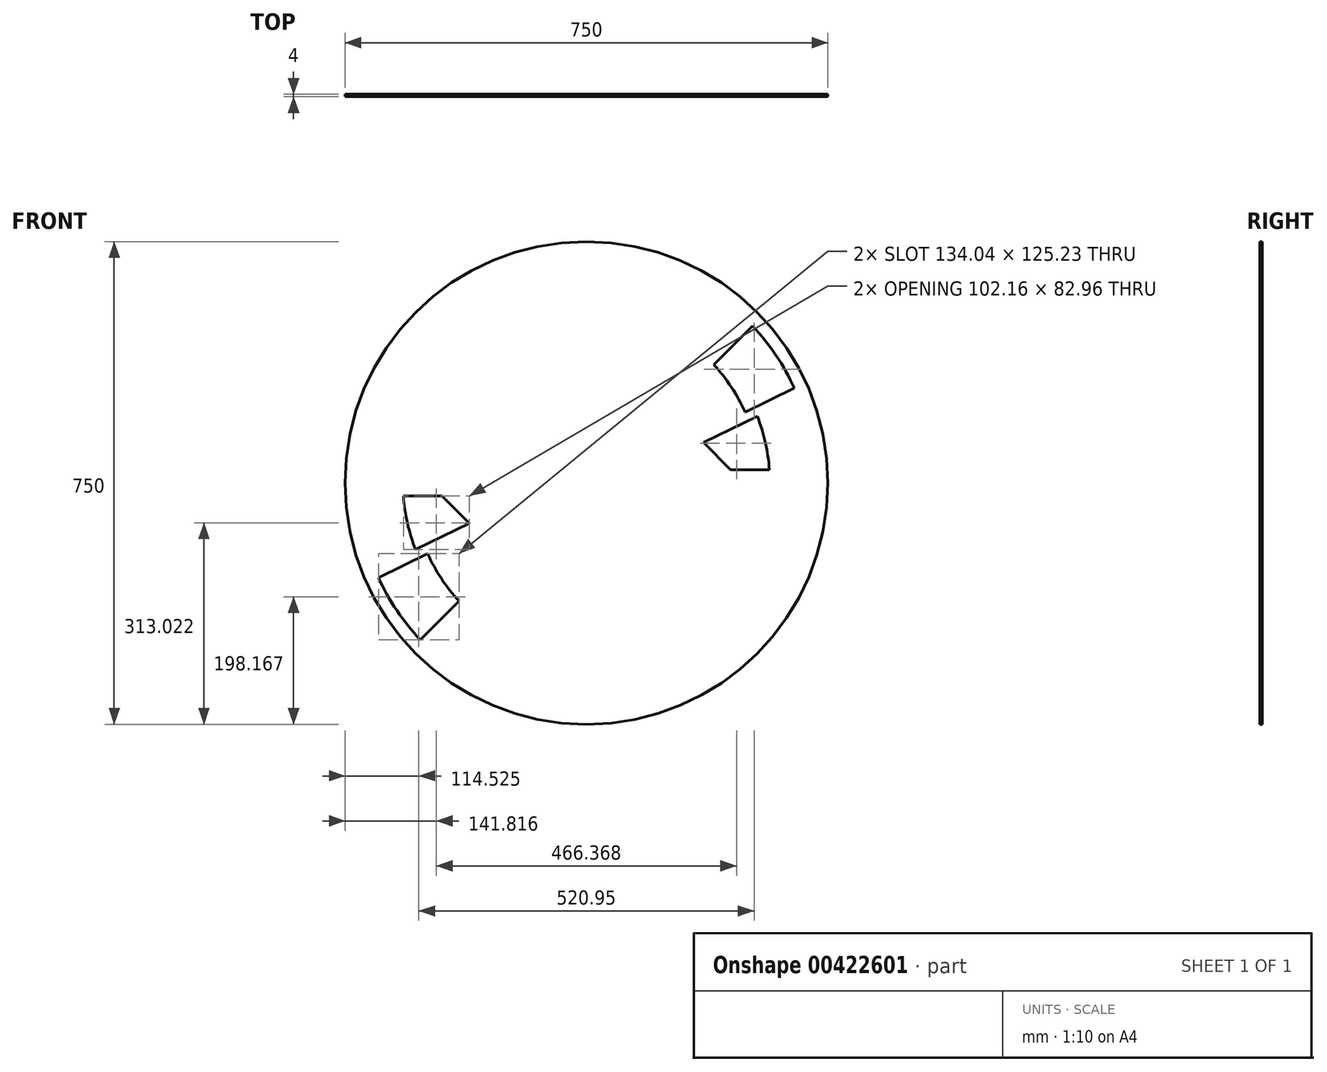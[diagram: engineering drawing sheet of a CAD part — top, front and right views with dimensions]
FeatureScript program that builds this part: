
annotation { "Feature Type Name" : "Feature", "Feature Type Description" : "" }
export const myFeature = defineFeature(function(context is Context, id is Id, definition is map)
    precondition{}
    {
        {
            var Q0;
            Q0=qCreatedBy(makeId("Front.planeOp"),FACE);
            var sketch = newSketch(context, id + "F0", { "sketchPlane" : qUnion([Q0])});
            skLineSegment(sketch, "E0", {"start": v(-123, -114.98) * mm, "end": v(-227.04, -10.5) * mm});
            skLineSegment(sketch, "E1", {"start": v(-227.04, -10.5) * mm, "end": v(-227.04, 10.5) * mm});
            skLineSegment(sketch, "E2", {"start": v(-227.04, 10.5) * mm, "end": v(-123.04, 115.02) * mm});
            skLineSegment(sketch, "E3", {"start": v(-123.04, 115.02) * mm, "end": v(122.96, 115.02) * mm});
            skLineSegment(sketch, "E4", {"start": v(122.96, 115.02) * mm, "end": v(226.96, 10.5) * mm});
            skLineSegment(sketch, "E5", {"start": v(226.96, 10.5) * mm, "end": v(226.96, -10.5) * mm});
            skLineSegment(sketch, "E6", {"start": v(226.96, -10.5) * mm, "end": v(123, -115.06) * mm});
            skLineSegment(sketch, "E7", {"start": v(123, -115.06) * mm, "end": v(-123, -114.98) * mm});
            skPoint(sketch, "E8.startSnap0", {"position": v(226.96, 0) * mm});
            skPoint(sketch, "E8.endSnap0", {"position": v(-227.04, 0) * mm});
            skPoint(sketch, "E9.endSnap0", {"position": v(0, -115.02) * mm});
            skPoint(sketch, "E10", {"position": v(0, 0) * mm});
            skLineSegment(sketch, "E11", {"start": v(0, -317.44) * mm, "end": v(0, 323.8) * mm, "construction": true});
            skLineSegment(sketch, "E12", {"start": v(439.72, 0) * mm, "end": v(-379.77, 0) * mm, "construction": true});
            skPoint(sketch, "E13", {"position": v(0, 115.02) * mm});
            skSolve(sketch);
        }
        {
            var Q0;
            Q0=qCreatedBy(makeId("Front.planeOp"),FACE);
            var sketch = newSketch(context, id + "F1", { "sketchPlane" : qUnion([Q0])});
            skLineSegment(sketch, "E14.bottom", {"start": v(-420, 150) * mm, "end": v(-250, 150) * mm});
            skLineSegment(sketch, "E14.top", {"start": v(-420, 350) * mm, "end": v(-250, 350) * mm});
            skLineSegment(sketch, "E14.left", {"start": v(-420, 150) * mm, "end": v(-420, 350) * mm});
            skLineSegment(sketch, "E14.right", {"start": v(-250, 150) * mm, "end": v(-250, 350) * mm});
            skPoint(sketch, "E15.0", {"position": v(0, -115.03) * mm});
            skPoint(sketch, "E16.0", {"position": v(-195.63, 123.06) * mm});
            skPoint(sketch, "E17.0", {"position": v(-424.13, 9.56) * mm});
            skPoint(sketch, "E18.0", {"position": v(225.44, 0) * mm});
            skLineSegment(sketch, "E19", {"start": v(0, -244.95) * mm, "end": v(0, 298.47) * mm, "construction": true});
            skLineSegment(sketch, "E20", {"start": v(303.44, 0) * mm, "end": v(-317.51, 0) * mm, "construction": true});
            skLineSegment(sketch, "E21.MirrorCS", {"start": v(250, 150) * mm, "end": v(250, 350) * mm});
            skLineSegment(sketch, "E22.MirrorCS", {"start": v(420, 150) * mm, "end": v(250, 150) * mm});
            skLineSegment(sketch, "E23.MirrorCS", {"start": v(420, 150) * mm, "end": v(420, 350) * mm});
            skLineSegment(sketch, "E24.MirrorCS", {"start": v(420, 350) * mm, "end": v(250, 350) * mm});
            skLineSegment(sketch, "E25.MirrorCS", {"start": v(-420, -150) * mm, "end": v(-250, -150) * mm});
            skLineSegment(sketch, "E26.MirrorCS", {"start": v(-420, -150) * mm, "end": v(-420, -350) * mm});
            skLineSegment(sketch, "E27.MirrorCS", {"start": v(-420, -350) * mm, "end": v(-250, -350) * mm});
            skLineSegment(sketch, "E28.MirrorCS", {"start": v(-250, -150) * mm, "end": v(-250, -350) * mm});
            skLineSegment(sketch, "E29.MirrorCS", {"start": v(250, -150) * mm, "end": v(250, -350) * mm});
            skLineSegment(sketch, "E30.MirrorCS", {"start": v(420, -350) * mm, "end": v(250, -350) * mm});
            skLineSegment(sketch, "E31.MirrorCS", {"start": v(420, -150) * mm, "end": v(420, -350) * mm});
            skLineSegment(sketch, "E32.MirrorCS", {"start": v(420, -150) * mm, "end": v(250, -150) * mm});
            skPoint(sketch, "E33", {"position": v(0, 0) * mm});
            skSolve(sketch);
        }
        {
            var Q0;
            Q0=qCreatedBy(makeId("Front.planeOp"),FACE);
            var sketch = newSketch(context, id + "F2", { "sketchPlane" : qUnion([Q0])});
            skCircle(sketch, "E34", {"center": v(0, 0) * mm, "radius": 375 * mm});
            skLineSegment(sketch, "E35", {"start": v(-224.15, 20.5) * mm, "end": v(-129.63, 115.49) * mm, "construction": true});
            skLineSegment(sketch, "E36", {"start": v(-129.63, 115.49) * mm, "end": v(-258, 243.85) * mm, "construction": true});
            skLineSegment(sketch, "E37", {"start": v(-224.15, 20.5) * mm, "end": v(-354.4, 20.5) * mm});
            skArc(sketch, "E38", {"start": v(-354.4, 20.5) * mm, "mid": v(325.93, -140.7) * mm, "end": v(-258, 243.85) * mm, "construction": true});
            skArc(sketch, "E39", {"start": v(-258, 243.85) * mm, "mid": v(-325.93, 140.7) * mm, "end": v(-354.4, 20.5) * mm, "construction": true});
            skLineSegment(sketch, "E40", {"start": v(0, 0) * mm, "end": v(-331.85, 331.85) * mm, "construction": true});
            skLineSegment(sketch, "E41", {"start": v(-176.89, 68) * mm, "end": v(-325.93, 140.7) * mm, "construction": true});
            skLineSegment(sketch, "E42.0", {"start": v(-171.67, 73.24) * mm, "end": v(-323.1, 147.1) * mm, "construction": true});
            skLineSegment(sketch, "E43.MirrorCS", {"start": v(-182.1, 62.75) * mm, "end": v(-252.03, 96.86) * mm, "construction": true});
            skPoint(sketch, "E44.orphan", {"position": v(-322.5, 146.81) * mm});
            skArc(sketch, "E45", {"start": v(-284.26, 20.5) * mm, "mid": v(261.25, -113.9) * mm, "end": v(-208.47, 194.33) * mm, "construction": true});
            skArc(sketch, "E46", {"start": v(-265.56, 103.46) * mm, "mid": v(-278.02, 62.68) * mm, "end": v(-284.26, 20.5) * mm, "construction": true});
            skArc(sketch, "E47", {"start": v(-260.15, 116.4) * mm, "mid": v(-262.93, 109.96) * mm, "end": v(-265.56, 103.46) * mm, "construction": true});
            skArc(sketch, "E48", {"start": v(-208.47, 194.33) * mm, "mid": v(-237.53, 157.5) * mm, "end": v(-260.15, 116.4) * mm, "construction": true});
            skArc(sketch, "E49", {"start": v(-197.86, 183.72) * mm, "mid": v(-225.3, 148.78) * mm, "end": v(-246.66, 109.81) * mm, "construction": true});
            skArc(sketch, "E50", {"start": v(-246.66, 109.81) * mm, "mid": v(-261.78, 66.13) * mm, "end": v(-269.22, 20.5) * mm, "construction": true});
            skLineSegment(sketch, "E51", {"start": v(-252.03, 96.86) * mm, "end": v(-328.65, 134.23) * mm, "construction": true});
            skArc(sketch, "E52", {"start": v(-269.22, 20.5) * mm, "mid": v(247.39, -108.16) * mm, "end": v(-197.86, 183.72) * mm, "construction": true});
            skLineSegment(sketch, "E53.MirrorCS", {"start": v(224.15, 20.5) * mm, "end": v(129.63, 115.49) * mm});
            skLineSegment(sketch, "E54.MirrorCS", {"start": v(171.67, 73.24) * mm, "end": v(323.1, 147.1) * mm});
            skLineSegment(sketch, "E55.MirrorCS", {"start": v(129.63, 115.49) * mm, "end": v(258, 243.85) * mm});
            skArc(sketch, "E56.MirrorCS", {"start": v(197.86, 183.72) * mm, "mid": v(225.3, 148.78) * mm, "end": v(246.66, 109.81) * mm});
            skArc(sketch, "E57.MirrorCS", {"start": v(208.47, 194.33) * mm, "mid": v(237.53, 157.5) * mm, "end": v(260.15, 116.4) * mm});
            skArc(sketch, "E58.MirrorCS", {"start": v(258, 243.85) * mm, "mid": v(325.93, 140.7) * mm, "end": v(354.4, 20.5) * mm});
            skLineSegment(sketch, "E59.MirrorCS", {"start": v(224.15, 20.5) * mm, "end": v(354.4, 20.5) * mm});
            skArc(sketch, "E60.MirrorCS", {"start": v(265.56, 103.46) * mm, "mid": v(278.02, 62.68) * mm, "end": v(284.26, 20.5) * mm});
            skArc(sketch, "E61.MirrorCS", {"start": v(246.66, 109.81) * mm, "mid": v(261.78, 66.13) * mm, "end": v(269.22, 20.5) * mm});
            skLineSegment(sketch, "E62.MirrorCS", {"start": v(182.1, 62.75) * mm, "end": v(252.03, 96.86) * mm});
            skLineSegment(sketch, "E63.MirrorCS", {"start": v(252.03, 96.86) * mm, "end": v(328.65, 134.23) * mm});
            skArc(sketch, "E64.MirrorCS", {"start": v(-258, -243.85) * mm, "mid": v(-325.93, -140.7) * mm, "end": v(-354.4, -20.5) * mm});
            skLineSegment(sketch, "E65.MirrorCS", {"start": v(-224.15, -20.5) * mm, "end": v(-354.4, -20.5) * mm});
            skArc(sketch, "E66.MirrorCS", {"start": v(-246.66, -109.81) * mm, "mid": v(-261.78, -66.13) * mm, "end": v(-269.22, -20.5) * mm});
            skArc(sketch, "E67.MirrorCS", {"start": v(-265.56, -103.46) * mm, "mid": v(-278.02, -62.68) * mm, "end": v(-284.26, -20.5) * mm});
            skLineSegment(sketch, "E68.MirrorCS", {"start": v(-252.03, -96.86) * mm, "end": v(-328.65, -134.23) * mm});
            skLineSegment(sketch, "E69.MirrorCS", {"start": v(-171.67, -73.24) * mm, "end": v(-323.1, -147.1) * mm});
            skLineSegment(sketch, "E70.MirrorCS", {"start": v(-182.1, -62.75) * mm, "end": v(-252.03, -96.86) * mm});
            skLineSegment(sketch, "E71.MirrorCS", {"start": v(-129.63, -115.49) * mm, "end": v(-258, -243.85) * mm});
            skArc(sketch, "E72.MirrorCS", {"start": v(-197.86, -183.72) * mm, "mid": v(-225.3, -148.78) * mm, "end": v(-246.66, -109.81) * mm});
            skArc(sketch, "E73.MirrorCS", {"start": v(-208.47, -194.33) * mm, "mid": v(-237.53, -157.5) * mm, "end": v(-260.15, -116.4) * mm});
            skLineSegment(sketch, "E74.MirrorCS", {"start": v(-224.15, -20.5) * mm, "end": v(-129.63, -115.49) * mm});
            skSolve(sketch);
        }
        {
            var Q0;
            Q0=makeQuery(id+"F2.imprint","IMPRINT",FACE,{"disambiguationData":[TD([[makeQuery(id+"F2.imprint","IMPRINT",EDGE,{"derivedFrom":sQuery(id+"F2.wireOp",EDGE,"E34")}),1.0]])]});
            var Q1;
            {var subQ3=sQuery(id+"F2.wireOp",EDGE,"E70.MirrorCS");Q1=makeQuery(id+"F2.imprint","IMPRINT",FACE,{"disambiguationData":[TD([[makeQuery(id+"F2.imprint","IMPRINT",EDGE,{"derivedFrom":subQ3}),1.0]])]});}
            var Q2;
            {var subQ5=sQuery(id+"F2.wireOp",EDGE,"E67.MirrorCS");Q2=makeQuery(id+"F2.imprint","IMPRINT",FACE,{"disambiguationData":[TD([[makeQuery(id+"F2.imprint","IMPRINT",EDGE,{"derivedFrom":subQ5}),-1.0]])]});}
            var Q3;
            {var subQ4=sQuery(id+"F2.wireOp",EDGE,"E68.MirrorCS");var subQ5=makeQuery(id+"F2.imprint","INTERSECT",VERTEX,{"derivedFrom":[sQuery(id+"F2.wireOp",EDGE,"E67.MirrorCS"),subQ4]});Q3=makeQuery(id+"F2.imprint","IMPRINT",FACE,{"disambiguationData":[TD([[makeQuery(id+"F2.imprint","IMPRINT",EDGE,{"disambiguationData":[TD([[subQ5,-1.0]])],"derivedFrom":subQ4}),1.0]])]});}
            var Q4;
            {var subQ0=sQuery(id+"F2.wireOp",EDGE,"E72.MirrorCS");Q4=makeQuery(id+"F2.imprint","IMPRINT",FACE,{"disambiguationData":[TD([[makeQuery(id+"F2.imprint","IMPRINT",EDGE,{"derivedFrom":subQ0}),1.0]])]});}
            var Q5;
            {var subQ0=sQuery(id+"F2.wireOp",EDGE,"E56.MirrorCS");Q5=makeQuery(id+"F2.imprint","IMPRINT",FACE,{"disambiguationData":[TD([[makeQuery(id+"F2.imprint","IMPRINT",EDGE,{"derivedFrom":subQ0}),1.0]])]});}
            var Q6;
            {var subQ3=sQuery(id+"F2.wireOp",EDGE,"E62.MirrorCS");Q6=makeQuery(id+"F2.imprint","IMPRINT",FACE,{"disambiguationData":[TD([[makeQuery(id+"F2.imprint","IMPRINT",EDGE,{"derivedFrom":subQ3}),1.0]])]});}
            var Q7;
            {var subQ0=sQuery(id+"F2.wireOp",EDGE,"E60.MirrorCS");Q7=makeQuery(id+"F2.imprint","IMPRINT",FACE,{"disambiguationData":[TD([[makeQuery(id+"F2.imprint","IMPRINT",EDGE,{"derivedFrom":subQ0}),-1.0]])]});}
            var Q8;
            {var subQ1=sQuery(id+"F2.wireOp",EDGE,"E54.MirrorCS");var subQ5=sQuery(id+"F2.wireOp",EDGE,"E58.MirrorCS");var subQ6=makeQuery(id+"F2.imprint","INTERSECT",VERTEX,{"derivedFrom":[subQ1,subQ5]});Q8=makeQuery(id+"F2.imprint","IMPRINT",FACE,{"disambiguationData":[TD([[makeQuery(id+"F2.imprint","IMPRINT",EDGE,{"disambiguationData":[TD([[subQ6,1.0]])],"derivedFrom":subQ1}),-1.0]])]});}
            extrude(context, id + "F3", {"entities" : qUnion([Q0, Q1, Q2, Q3, Q4, Q5, Q6, Q7, Q8]), "depth" : 4 * mm});
        }
    });
